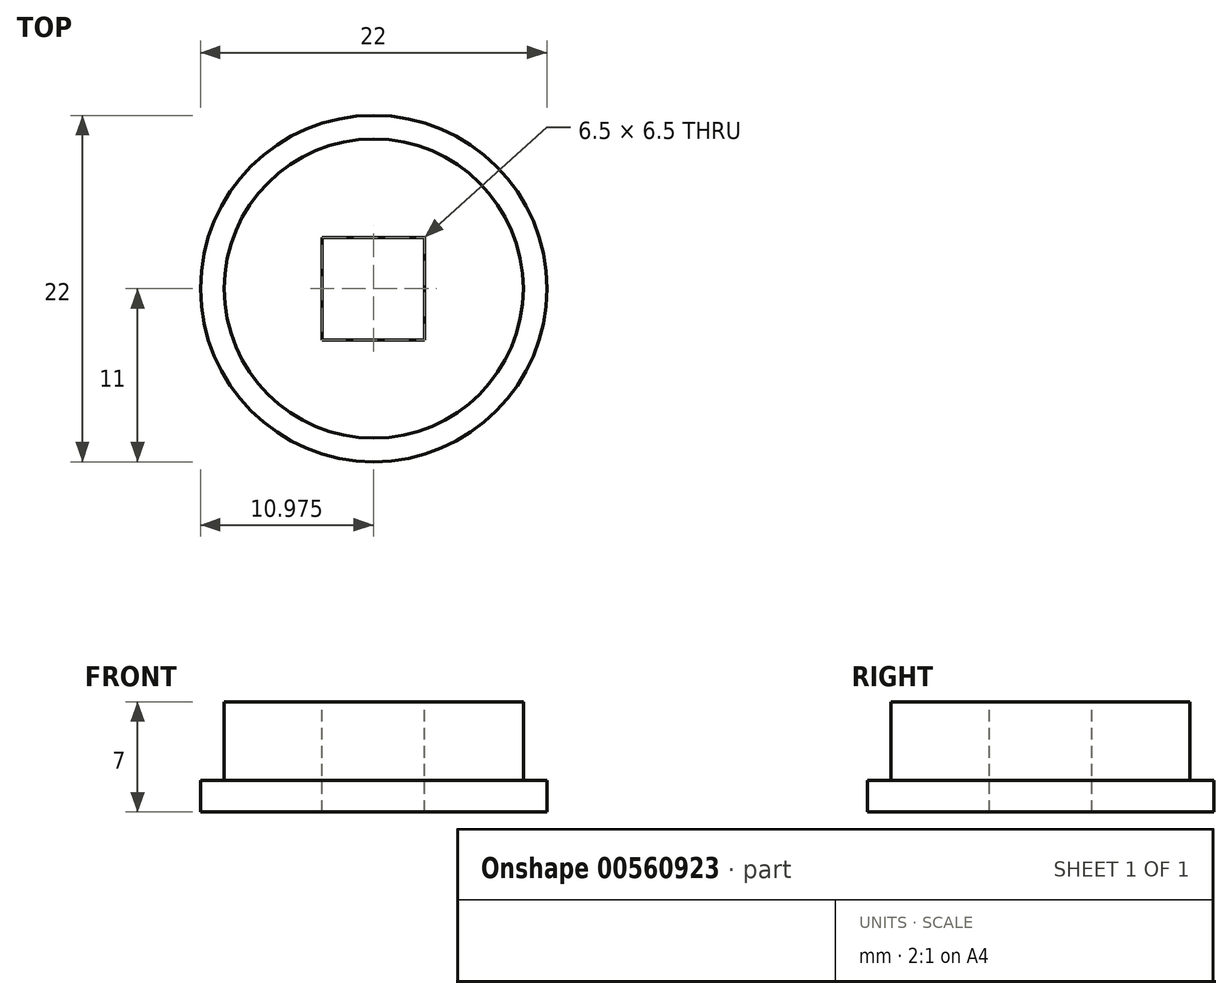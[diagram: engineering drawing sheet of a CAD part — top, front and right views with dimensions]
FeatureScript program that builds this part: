
annotation { "Feature Type Name" : "Feature", "Feature Type Description" : "" }
export const myFeature = defineFeature(function(context is Context, id is Id, definition is map)
    precondition{}
    {
        {
            var Q0;
            Q0=qCreatedBy(makeId("Top.planeOp"),FACE);
            var sketch = newSketch(context, id + "F0", { "sketchPlane" : qUnion([Q0])});
            skCircle(sketch, "E0", {"center": v(0, 0) * mm, "radius": 9.5 * mm});
            skCircle(sketch, "E1", {"center": v(0, 0) * mm, "radius": 11 * mm});
            skLineSegment(sketch, "E2.bottom", {"start": v(-3.28, 3.25) * mm, "end": v(3.23, 3.25) * mm});
            skLineSegment(sketch, "E2.top", {"start": v(-3.28, -3.25) * mm, "end": v(3.23, -3.25) * mm});
            skLineSegment(sketch, "E2.left", {"start": v(-3.28, 3.25) * mm, "end": v(-3.28, -3.25) * mm});
            skLineSegment(sketch, "E2.right", {"start": v(3.23, 3.25) * mm, "end": v(3.23, -3.25) * mm});
            skSolve(sketch);
        }
        {
            var Q0;
            Q0=makeQuery(id+"F0.imprint","IMPRINT",FACE,{"disambiguationData":[TD([[makeQuery(id+"F0.imprint","IMPRINT",EDGE,{"derivedFrom":sQuery(id+"F0.wireOp",EDGE,"E0")}),-1.0]])]});
            var Q1;
            Q1=makeQuery(id+"F0.imprint","IMPRINT",FACE,{"disambiguationData":[TD([[makeQuery(id+"F0.imprint","IMPRINT",EDGE,{"derivedFrom":sQuery(id+"F0.wireOp",EDGE,"E0")}),1.0]])]});
            extrude(context, id + "F1", {"entities" : qUnion([Q0, Q1]), "oppositeDirection" : true, "depth" : 2 * mm, "offsetDistance" : 25 * mm});
        }
        {
            var Q0;
            Q0=makeQuery(id+"F0.imprint","IMPRINT",FACE,{"disambiguationData":[TD([[makeQuery(id+"F0.imprint","IMPRINT",EDGE,{"derivedFrom":sQuery(id+"F0.wireOp",EDGE,"E0")}),1.0]])]});
            extrude(context, id + "F2", {"entities" : qUnion([Q0]), "operationType" : NewBodyOperationType.ADD, "depth" : 5 * mm, "offsetDistance" : 25 * mm});
        }
    });
